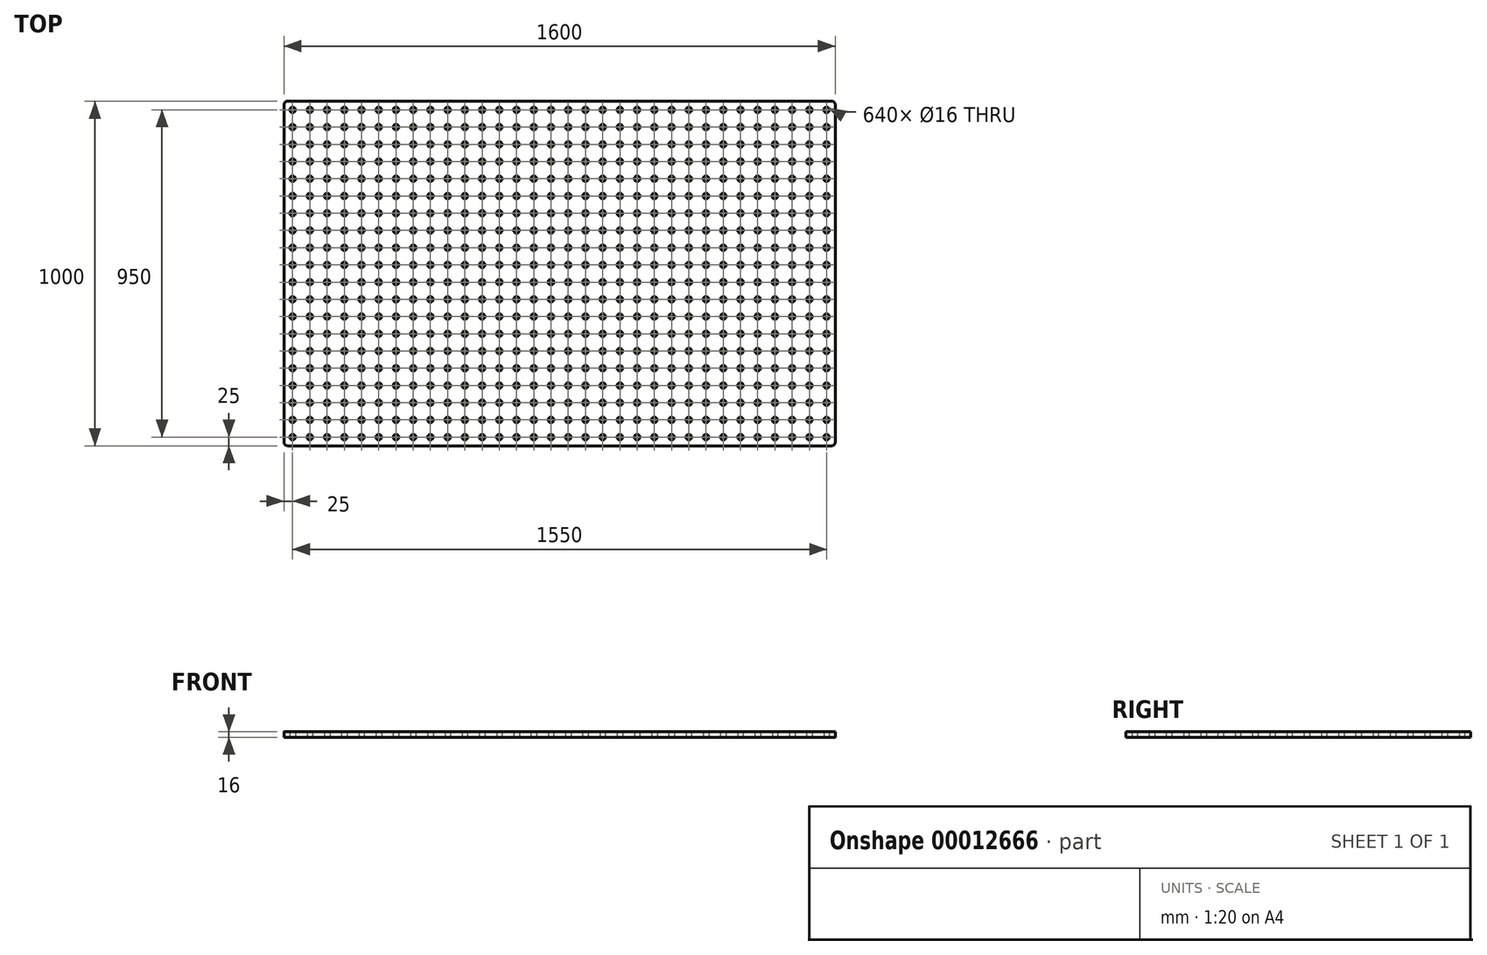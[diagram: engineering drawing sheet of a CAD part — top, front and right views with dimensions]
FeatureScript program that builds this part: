
annotation { "Feature Type Name" : "Feature", "Feature Type Description" : "" }
export const myFeature = defineFeature(function(context is Context, id is Id, definition is map)
    precondition{}
    {
        {
            var Q0;
            Q0=qCreatedBy(makeId("Top.planeOp"),FACE);
            var sketch = newSketch(context, id + "F0", { "sketchPlane" : qUnion([Q0])});
            skLineSegment(sketch, "E0.rect.top", {"start": v(-800, -500) * mm, "end": v(800, -500) * mm});
            skLineSegment(sketch, "E0.rect.left", {"start": v(-800, 500) * mm, "end": v(-800, -500) * mm});
            skLineSegment(sketch, "E0.rect.right", {"start": v(800, 500) * mm, "end": v(800, -500) * mm});
            skPoint(sketch, "E0.rect.middle", {"position": v(0, 0) * mm});
            skCircle(sketch, "E1", {"center": v(-775, 475) * mm, "radius": 8 * mm});
            skCircle(sketch, "E2", {"center": v(-725, 475) * mm, "radius": 8 * mm});
            skCircle(sketch, "E3", {"center": v(-675, 475) * mm, "radius": 8 * mm});
            skCircle(sketch, "E4", {"center": v(-625, 475) * mm, "radius": 8 * mm});
            skCircle(sketch, "E5", {"center": v(-575, 475) * mm, "radius": 8 * mm});
            skCircle(sketch, "E6", {"center": v(-525, 475) * mm, "radius": 8 * mm});
            skCircle(sketch, "E7", {"center": v(-475, 475) * mm, "radius": 8 * mm});
            skCircle(sketch, "E8", {"center": v(-425, 475) * mm, "radius": 8 * mm});
            skCircle(sketch, "E9", {"center": v(-375, 475) * mm, "radius": 8 * mm});
            skCircle(sketch, "E10", {"center": v(-325, 475) * mm, "radius": 8 * mm});
            skCircle(sketch, "E11", {"center": v(-275, 475) * mm, "radius": 8 * mm});
            skCircle(sketch, "E12", {"center": v(-225, 475) * mm, "radius": 8 * mm});
            skCircle(sketch, "E13", {"center": v(-125, 475) * mm, "radius": 8 * mm});
            skCircle(sketch, "E14", {"center": v(-75, 475) * mm, "radius": 8 * mm});
            skCircle(sketch, "E15", {"center": v(-25, 475) * mm, "radius": 8 * mm});
            skCircle(sketch, "E16", {"center": v(25, 475) * mm, "radius": 8 * mm});
            skCircle(sketch, "E17", {"center": v(75, 475) * mm, "radius": 8 * mm});
            skCircle(sketch, "E18", {"center": v(125, 475) * mm, "radius": 8 * mm});
            skCircle(sketch, "E19", {"center": v(175, 475) * mm, "radius": 8 * mm});
            skCircle(sketch, "E20", {"center": v(225, 475) * mm, "radius": 8 * mm});
            skCircle(sketch, "E21", {"center": v(275, 475) * mm, "radius": 8 * mm});
            skCircle(sketch, "E22", {"center": v(325, 475) * mm, "radius": 8 * mm});
            skCircle(sketch, "E23", {"center": v(375, 475) * mm, "radius": 8 * mm});
            skCircle(sketch, "E24", {"center": v(425, 475) * mm, "radius": 8 * mm});
            skCircle(sketch, "E25", {"center": v(475, 475) * mm, "radius": 8 * mm});
            skCircle(sketch, "E26", {"center": v(525, 475) * mm, "radius": 8 * mm});
            skCircle(sketch, "E27", {"center": v(575, 475) * mm, "radius": 8 * mm});
            skCircle(sketch, "E28", {"center": v(625, 475) * mm, "radius": 8 * mm});
            skCircle(sketch, "E29", {"center": v(675, 475) * mm, "radius": 8 * mm});
            skCircle(sketch, "E30", {"center": v(725, 475) * mm, "radius": 8 * mm});
            skCircle(sketch, "E31", {"center": v(775, 475) * mm, "radius": 8 * mm});
            skCircle(sketch, "E32", {"center": v(-175, 475) * mm, "radius": 8 * mm});
            skLineSegment(sketch, "E33", {"start": v(-800, 0) * mm, "end": v(800, 0) * mm, "construction": true});
            skLineSegment(sketch, "E34", {"start": v(-800, 500) * mm, "end": v(800, 500) * mm});
            skCircle(sketch, "E35.0.MirrorC", {"center": v(275, 425) * mm, "radius": 8 * mm});
            skCircle(sketch, "E35.1.MirrorC", {"center": v(725, 425) * mm, "radius": 8 * mm});
            skCircle(sketch, "E35.2.MirrorC", {"center": v(775, 425) * mm, "radius": 8 * mm});
            skCircle(sketch, "E35.3.MirrorC", {"center": v(325, 425) * mm, "radius": 8 * mm});
            skCircle(sketch, "E35.4.MirrorC", {"center": v(-275, 425) * mm, "radius": 8 * mm});
            skCircle(sketch, "E35.5.MirrorC", {"center": v(675, 425) * mm, "radius": 8 * mm});
            skCircle(sketch, "E35.6.MirrorC", {"center": v(575, 425) * mm, "radius": 8 * mm});
            skCircle(sketch, "E35.7.MirrorC", {"center": v(-575, 425) * mm, "radius": 8 * mm});
            skCircle(sketch, "E35.8.MirrorC", {"center": v(-25, 425) * mm, "radius": 8 * mm});
            skCircle(sketch, "E35.9.MirrorC", {"center": v(75, 425) * mm, "radius": 8 * mm});
            skCircle(sketch, "E35.10.MirrorC", {"center": v(-175, 425) * mm, "radius": 8 * mm});
            skCircle(sketch, "E35.11.MirrorC", {"center": v(25, 425) * mm, "radius": 8 * mm});
            skCircle(sketch, "E35.12.MirrorC", {"center": v(175, 425) * mm, "radius": 8 * mm});
            skCircle(sketch, "E35.13.MirrorC", {"center": v(475, 425) * mm, "radius": 8 * mm});
            skCircle(sketch, "E35.14.MirrorC", {"center": v(-525, 425) * mm, "radius": 8 * mm});
            skCircle(sketch, "E35.15.MirrorC", {"center": v(-225, 425) * mm, "radius": 8 * mm});
            skCircle(sketch, "E35.16.MirrorC", {"center": v(-75, 425) * mm, "radius": 8 * mm});
            skCircle(sketch, "E35.17.MirrorC", {"center": v(375, 425) * mm, "radius": 8 * mm});
            skCircle(sketch, "E35.18.MirrorC", {"center": v(-325, 425) * mm, "radius": 8 * mm});
            skCircle(sketch, "E35.19.MirrorC", {"center": v(125, 425) * mm, "radius": 8 * mm});
            skCircle(sketch, "E35.20.MirrorC", {"center": v(-125, 425) * mm, "radius": 8 * mm});
            skCircle(sketch, "E35.21.MirrorC", {"center": v(525, 425) * mm, "radius": 8 * mm});
            skCircle(sketch, "E35.22.MirrorC", {"center": v(225, 425) * mm, "radius": 8 * mm});
            skCircle(sketch, "E35.23.MirrorC", {"center": v(625, 425) * mm, "radius": 8 * mm});
            skCircle(sketch, "E35.24.MirrorC", {"center": v(-725, 425) * mm, "radius": 8 * mm});
            skCircle(sketch, "E35.25.MirrorC", {"center": v(-775, 425) * mm, "radius": 8 * mm});
            skCircle(sketch, "E35.26.MirrorC", {"center": v(-625, 425) * mm, "radius": 8 * mm});
            skCircle(sketch, "E35.27.MirrorC", {"center": v(-675, 425) * mm, "radius": 8 * mm});
            skCircle(sketch, "E35.28.MirrorC", {"center": v(-425, 425) * mm, "radius": 8 * mm});
            skCircle(sketch, "E35.29.MirrorC", {"center": v(-475, 425) * mm, "radius": 8 * mm});
            skCircle(sketch, "E35.30.MirrorC", {"center": v(-375, 425) * mm, "radius": 8 * mm});
            skCircle(sketch, "E35.31.MirrorC", {"center": v(425, 425) * mm, "radius": 8 * mm});
            skCircle(sketch, "E36.0.MirrorC", {"center": v(275, 325) * mm, "radius": 8 * mm});
            skCircle(sketch, "E36.1.MirrorC", {"center": v(375, 375) * mm, "radius": 8 * mm});
            skCircle(sketch, "E36.2.MirrorC", {"center": v(725, 375) * mm, "radius": 8 * mm});
            skCircle(sketch, "E36.3.MirrorC", {"center": v(525, 325) * mm, "radius": 8 * mm});
            skCircle(sketch, "E36.4.MirrorC", {"center": v(575, 375) * mm, "radius": 8 * mm});
            skCircle(sketch, "E36.5.MirrorC", {"center": v(225, 375) * mm, "radius": 8 * mm});
            skCircle(sketch, "E36.6.MirrorC", {"center": v(-775, 375) * mm, "radius": 8 * mm});
            skCircle(sketch, "E36.7.MirrorC", {"center": v(75, 375) * mm, "radius": 8 * mm});
            skCircle(sketch, "E36.8.MirrorC", {"center": v(675, 325) * mm, "radius": 8 * mm});
            skCircle(sketch, "E36.9.MirrorC", {"center": v(425, 375) * mm, "radius": 8 * mm});
            skCircle(sketch, "E36.10.MirrorC", {"center": v(-225, 375) * mm, "radius": 8 * mm});
            skCircle(sketch, "E36.11.MirrorC", {"center": v(175, 325) * mm, "radius": 8 * mm});
            skCircle(sketch, "E36.12.MirrorC", {"center": v(-725, 375) * mm, "radius": 8 * mm});
            skCircle(sketch, "E36.13.MirrorC", {"center": v(625, 325) * mm, "radius": 8 * mm});
            skCircle(sketch, "E36.14.MirrorC", {"center": v(-25, 375) * mm, "radius": 8 * mm});
            skCircle(sketch, "E36.15.MirrorC", {"center": v(-75, 375) * mm, "radius": 8 * mm});
            skCircle(sketch, "E36.16.MirrorC", {"center": v(275, 375) * mm, "radius": 8 * mm});
            skCircle(sketch, "E36.17.MirrorC", {"center": v(225, 325) * mm, "radius": 8 * mm});
            skCircle(sketch, "E36.18.MirrorC", {"center": v(-275, 375) * mm, "radius": 8 * mm});
            skCircle(sketch, "E36.19.MirrorC", {"center": v(-125, 375) * mm, "radius": 8 * mm});
            skCircle(sketch, "E36.20.MirrorC", {"center": v(425, 325) * mm, "radius": 8 * mm});
            skCircle(sketch, "E36.21.MirrorC", {"center": v(-575, 375) * mm, "radius": 8 * mm});
            skCircle(sketch, "E36.22.MirrorC", {"center": v(575, 325) * mm, "radius": 8 * mm});
            skCircle(sketch, "E36.23.MirrorC", {"center": v(625, 375) * mm, "radius": 8 * mm});
            skCircle(sketch, "E36.24.MirrorC", {"center": v(475, 375) * mm, "radius": 8 * mm});
            skCircle(sketch, "E36.25.MirrorC", {"center": v(-475, 375) * mm, "radius": 8 * mm});
            skCircle(sketch, "E36.26.MirrorC", {"center": v(75, 325) * mm, "radius": 8 * mm});
            skCircle(sketch, "E36.27.MirrorC", {"center": v(525, 375) * mm, "radius": 8 * mm});
            skCircle(sketch, "E36.28.MirrorC", {"center": v(675, 375) * mm, "radius": 8 * mm});
            skCircle(sketch, "E36.29.MirrorC", {"center": v(475, 325) * mm, "radius": 8 * mm});
            skCircle(sketch, "E36.30.MirrorC", {"center": v(175, 375) * mm, "radius": 8 * mm});
            skCircle(sketch, "E36.31.MirrorC", {"center": v(-525, 325) * mm, "radius": 8 * mm});
            skCircle(sketch, "E36.32.MirrorC", {"center": v(375, 325) * mm, "radius": 8 * mm});
            skCircle(sketch, "E36.33.MirrorC", {"center": v(125, 375) * mm, "radius": 8 * mm});
            skCircle(sketch, "E36.34.MirrorC", {"center": v(-25, 325) * mm, "radius": 8 * mm});
            skCircle(sketch, "E36.35.MirrorC", {"center": v(125, 325) * mm, "radius": 8 * mm});
            skCircle(sketch, "E36.36.MirrorC", {"center": v(25, 325) * mm, "radius": 8 * mm});
            skCircle(sketch, "E36.37.MirrorC", {"center": v(-425, 375) * mm, "radius": 8 * mm});
            skCircle(sketch, "E36.38.MirrorC", {"center": v(-625, 375) * mm, "radius": 8 * mm});
            skCircle(sketch, "E36.39.MirrorC", {"center": v(775, 325) * mm, "radius": 8 * mm});
            skCircle(sketch, "E36.40.MirrorC", {"center": v(-575, 325) * mm, "radius": 8 * mm});
            skCircle(sketch, "E36.41.MirrorC", {"center": v(-775, 325) * mm, "radius": 8 * mm});
            skCircle(sketch, "E36.42.MirrorC", {"center": v(-725, 325) * mm, "radius": 8 * mm});
            skCircle(sketch, "E36.43.MirrorC", {"center": v(-375, 375) * mm, "radius": 8 * mm});
            skCircle(sketch, "E36.44.MirrorC", {"center": v(-525, 375) * mm, "radius": 8 * mm});
            skCircle(sketch, "E36.45.MirrorC", {"center": v(725, 325) * mm, "radius": 8 * mm});
            skCircle(sketch, "E36.46.MirrorC", {"center": v(-625, 325) * mm, "radius": 8 * mm});
            skCircle(sketch, "E36.47.MirrorC", {"center": v(-175, 325) * mm, "radius": 8 * mm});
            skCircle(sketch, "E36.48.MirrorC", {"center": v(-275, 325) * mm, "radius": 8 * mm});
            skCircle(sketch, "E36.49.MirrorC", {"center": v(-125, 325) * mm, "radius": 8 * mm});
            skCircle(sketch, "E36.50.MirrorC", {"center": v(-225, 325) * mm, "radius": 8 * mm});
            skCircle(sketch, "E36.51.MirrorC", {"center": v(-75, 325) * mm, "radius": 8 * mm});
            skCircle(sketch, "E36.52.MirrorC", {"center": v(325, 325) * mm, "radius": 8 * mm});
            skCircle(sketch, "E36.53.MirrorC", {"center": v(775, 375) * mm, "radius": 8 * mm});
            skCircle(sketch, "E36.54.MirrorC", {"center": v(-325, 375) * mm, "radius": 8 * mm});
            skCircle(sketch, "E36.55.MirrorC", {"center": v(-375, 325) * mm, "radius": 8 * mm});
            skCircle(sketch, "E36.56.MirrorC", {"center": v(-475, 325) * mm, "radius": 8 * mm});
            skCircle(sketch, "E36.57.MirrorC", {"center": v(-325, 325) * mm, "radius": 8 * mm});
            skCircle(sketch, "E36.58.MirrorC", {"center": v(-675, 375) * mm, "radius": 8 * mm});
            skCircle(sketch, "E36.59.MirrorC", {"center": v(25, 375) * mm, "radius": 8 * mm});
            skCircle(sketch, "E36.60.MirrorC", {"center": v(-175, 375) * mm, "radius": 8 * mm});
            skCircle(sketch, "E36.61.MirrorC", {"center": v(-675, 325) * mm, "radius": 8 * mm});
            skCircle(sketch, "E36.62.MirrorC", {"center": v(325, 375) * mm, "radius": 8 * mm});
            skCircle(sketch, "E36.63.MirrorC", {"center": v(-425, 325) * mm, "radius": 8 * mm});
            skCircle(sketch, "E37.0.MirrorC", {"center": v(-675, 275) * mm, "radius": 8 * mm});
            skCircle(sketch, "E37.1.MirrorC", {"center": v(475, 275) * mm, "radius": 8 * mm});
            skCircle(sketch, "E37.2.MirrorC", {"center": v(725, 275) * mm, "radius": 8 * mm});
            skCircle(sketch, "E37.3.MirrorC", {"center": v(425, 175) * mm, "radius": 8 * mm});
            skCircle(sketch, "E37.4.MirrorC", {"center": v(625, 275) * mm, "radius": 8 * mm});
            skCircle(sketch, "E37.5.MirrorC", {"center": v(-225, 175) * mm, "radius": 8 * mm});
            skCircle(sketch, "E37.6.MirrorC", {"center": v(175, 125) * mm, "radius": 8 * mm});
            skCircle(sketch, "E37.7.MirrorC", {"center": v(-25, 225) * mm, "radius": 8 * mm});
            skCircle(sketch, "E37.8.MirrorC", {"center": v(-75, 175) * mm, "radius": 8 * mm});
            skCircle(sketch, "E37.9.MirrorC", {"center": v(275, 175) * mm, "radius": 8 * mm});
            skCircle(sketch, "E37.10.MirrorC", {"center": v(225, 125) * mm, "radius": 8 * mm});
            skCircle(sketch, "E37.11.MirrorC", {"center": v(325, 225) * mm, "radius": 8 * mm});
            skCircle(sketch, "E37.12.MirrorC", {"center": v(-625, 275) * mm, "radius": 8 * mm});
            skCircle(sketch, "E37.13.MirrorC", {"center": v(175, 225) * mm, "radius": 8 * mm});
            skCircle(sketch, "E37.14.MirrorC", {"center": v(-375, 225) * mm, "radius": 8 * mm});
            skCircle(sketch, "E37.15.MirrorC", {"center": v(525, 225) * mm, "radius": 8 * mm});
            skCircle(sketch, "E37.16.MirrorC", {"center": v(25, 225) * mm, "radius": 8 * mm});
            skCircle(sketch, "E37.17.MirrorC", {"center": v(475, 175) * mm, "radius": 8 * mm});
            skCircle(sketch, "E37.18.MirrorC", {"center": v(175, 275) * mm, "radius": 8 * mm});
            skCircle(sketch, "E37.19.MirrorC", {"center": v(-475, 175) * mm, "radius": 8 * mm});
            skCircle(sketch, "E37.20.MirrorC", {"center": v(75, 125) * mm, "radius": 8 * mm});
            skCircle(sketch, "E37.21.MirrorC", {"center": v(675, 225) * mm, "radius": 8 * mm});
            skCircle(sketch, "E37.22.MirrorC", {"center": v(-525, 225) * mm, "radius": 8 * mm});
            skCircle(sketch, "E37.23.MirrorC", {"center": v(-175, 225) * mm, "radius": 8 * mm});
            skCircle(sketch, "E37.24.MirrorC", {"center": v(-525, 175) * mm, "radius": 8 * mm});
            skCircle(sketch, "E37.25.MirrorC", {"center": v(-725, 225) * mm, "radius": 8 * mm});
            skCircle(sketch, "E37.26.MirrorC", {"center": v(-375, 175) * mm, "radius": 8 * mm});
            skCircle(sketch, "E37.27.MirrorC", {"center": v(125, 125) * mm, "radius": 8 * mm});
            skCircle(sketch, "E37.28.MirrorC", {"center": v(-425, 275) * mm, "radius": 8 * mm});
            skCircle(sketch, "E37.29.MirrorC", {"center": v(-275, 125) * mm, "radius": 8 * mm});
            skCircle(sketch, "E37.30.MirrorC", {"center": v(-125, 125) * mm, "radius": 8 * mm});
            skCircle(sketch, "E37.31.MirrorC", {"center": v(-225, 125) * mm, "radius": 8 * mm});
            skCircle(sketch, "E37.32.MirrorC", {"center": v(275, 225) * mm, "radius": 8 * mm});
            skCircle(sketch, "E37.33.MirrorC", {"center": v(275, 275) * mm, "radius": 8 * mm});
            skCircle(sketch, "E37.34.MirrorC", {"center": v(-275, 275) * mm, "radius": 8 * mm});
            skCircle(sketch, "E37.35.MirrorC", {"center": v(375, 275) * mm, "radius": 8 * mm});
            skCircle(sketch, "E37.36.MirrorC", {"center": v(325, 125) * mm, "radius": 8 * mm});
            skCircle(sketch, "E37.37.MirrorC", {"center": v(-325, 175) * mm, "radius": 8 * mm});
            skCircle(sketch, "E37.38.MirrorC", {"center": v(775, 175) * mm, "radius": 8 * mm});
            skCircle(sketch, "E37.39.MirrorC", {"center": v(-375, 125) * mm, "radius": 8 * mm});
            skCircle(sketch, "E37.40.MirrorC", {"center": v(-325, 125) * mm, "radius": 8 * mm});
            skCircle(sketch, "E37.41.MirrorC", {"center": v(-475, 125) * mm, "radius": 8 * mm});
            skCircle(sketch, "E37.42.MirrorC", {"center": v(-425, 125) * mm, "radius": 8 * mm});
            skCircle(sketch, "E37.43.MirrorC", {"center": v(-575, 125) * mm, "radius": 8 * mm});
            skCircle(sketch, "E37.44.MirrorC", {"center": v(-525, 125) * mm, "radius": 8 * mm});
            skCircle(sketch, "E37.45.MirrorC", {"center": v(-675, 125) * mm, "radius": 8 * mm});
            skCircle(sketch, "E37.46.MirrorC", {"center": v(-625, 125) * mm, "radius": 8 * mm});
            skCircle(sketch, "E37.47.MirrorC", {"center": v(-775, 125) * mm, "radius": 8 * mm});
            skCircle(sketch, "E37.48.MirrorC", {"center": v(-725, 125) * mm, "radius": 8 * mm});
            skCircle(sketch, "E37.49.MirrorC", {"center": v(325, 175) * mm, "radius": 8 * mm});
            skCircle(sketch, "E37.50.MirrorC", {"center": v(375, 125) * mm, "radius": 8 * mm});
            skCircle(sketch, "E37.51.MirrorC", {"center": v(125, 175) * mm, "radius": 8 * mm});
            skCircle(sketch, "E37.52.MirrorC", {"center": v(375, 225) * mm, "radius": 8 * mm});
            skCircle(sketch, "E37.53.MirrorC", {"center": v(225, 275) * mm, "radius": 8 * mm});
            skCircle(sketch, "E37.54.MirrorC", {"center": v(125, 225) * mm, "radius": 8 * mm});
            skCircle(sketch, "E37.55.MirrorC", {"center": v(-575, 225) * mm, "radius": 8 * mm});
            skCircle(sketch, "E37.56.MirrorC", {"center": v(-425, 225) * mm, "radius": 8 * mm});
            skCircle(sketch, "E37.57.MirrorC", {"center": v(775, 225) * mm, "radius": 8 * mm});
            skCircle(sketch, "E37.58.MirrorC", {"center": v(625, 175) * mm, "radius": 8 * mm});
            skCircle(sketch, "E37.59.MirrorC", {"center": v(225, 225) * mm, "radius": 8 * mm});
            skCircle(sketch, "E37.60.MirrorC", {"center": v(575, 125) * mm, "radius": 8 * mm});
            skCircle(sketch, "E37.61.MirrorC", {"center": v(-575, 175) * mm, "radius": 8 * mm});
            skCircle(sketch, "E37.62.MirrorC", {"center": v(425, 125) * mm, "radius": 8 * mm});
            skCircle(sketch, "E37.63.MirrorC", {"center": v(-125, 175) * mm, "radius": 8 * mm});
            skCircle(sketch, "E37.64.MirrorC", {"center": v(-275, 175) * mm, "radius": 8 * mm});
            skCircle(sketch, "E37.65.MirrorC", {"center": v(725, 225) * mm, "radius": 8 * mm});
            skCircle(sketch, "E37.66.MirrorC", {"center": v(-275, 225) * mm, "radius": 8 * mm});
            skCircle(sketch, "E37.67.MirrorC", {"center": v(-25, 275) * mm, "radius": 8 * mm});
            skCircle(sketch, "E37.68.MirrorC", {"center": v(-225, 275) * mm, "radius": 8 * mm});
            skCircle(sketch, "E37.69.MirrorC", {"center": v(475, 225) * mm, "radius": 8 * mm});
            skCircle(sketch, "E37.70.MirrorC", {"center": v(-575, 275) * mm, "radius": 8 * mm});
            skCircle(sketch, "E37.71.MirrorC", {"center": v(-475, 275) * mm, "radius": 8 * mm});
            skCircle(sketch, "E37.72.MirrorC", {"center": v(675, 275) * mm, "radius": 8 * mm});
            skCircle(sketch, "E37.73.MirrorC", {"center": v(-625, 175) * mm, "radius": 8 * mm});
            skCircle(sketch, "E37.74.MirrorC", {"center": v(-175, 175) * mm, "radius": 8 * mm});
            skCircle(sketch, "E37.75.MirrorC", {"center": v(725, 125) * mm, "radius": 8 * mm});
            skCircle(sketch, "E37.76.MirrorC", {"center": v(-75, 125) * mm, "radius": 8 * mm});
            skCircle(sketch, "E37.77.MirrorC", {"center": v(-25, 175) * mm, "radius": 8 * mm});
            skCircle(sketch, "E37.78.MirrorC", {"center": v(625, 125) * mm, "radius": 8 * mm});
            skCircle(sketch, "E37.79.MirrorC", {"center": v(-775, 225) * mm, "radius": 8 * mm});
            skCircle(sketch, "E37.80.MirrorC", {"center": v(-725, 175) * mm, "radius": 8 * mm});
            skCircle(sketch, "E37.81.MirrorC", {"center": v(-625, 225) * mm, "radius": 8 * mm});
            skCircle(sketch, "E37.82.MirrorC", {"center": v(575, 275) * mm, "radius": 8 * mm});
            skCircle(sketch, "E37.83.MirrorC", {"center": v(-325, 225) * mm, "radius": 8 * mm});
            skCircle(sketch, "E37.84.MirrorC", {"center": v(675, 125) * mm, "radius": 8 * mm});
            skCircle(sketch, "E37.85.MirrorC", {"center": v(-125, 225) * mm, "radius": 8 * mm});
            skCircle(sketch, "E37.86.MirrorC", {"center": v(-775, 275) * mm, "radius": 8 * mm});
            skCircle(sketch, "E37.87.MirrorC", {"center": v(125, 275) * mm, "radius": 8 * mm});
            skCircle(sketch, "E37.88.MirrorC", {"center": v(-25, 125) * mm, "radius": 8 * mm});
            skCircle(sketch, "E37.89.MirrorC", {"center": v(425, 225) * mm, "radius": 8 * mm});
            skCircle(sketch, "E37.90.MirrorC", {"center": v(25, 125) * mm, "radius": 8 * mm});
            skCircle(sketch, "E37.91.MirrorC", {"center": v(-675, 225) * mm, "radius": 8 * mm});
            skCircle(sketch, "E37.92.MirrorC", {"center": v(75, 175) * mm, "radius": 8 * mm});
            skCircle(sketch, "E37.93.MirrorC", {"center": v(275, 125) * mm, "radius": 8 * mm});
            skCircle(sketch, "E37.94.MirrorC", {"center": v(525, 125) * mm, "radius": 8 * mm});
            skCircle(sketch, "E37.95.MirrorC", {"center": v(175, 175) * mm, "radius": 8 * mm});
            skCircle(sketch, "E37.96.MirrorC", {"center": v(-225, 225) * mm, "radius": 8 * mm});
            skCircle(sketch, "E37.97.MirrorC", {"center": v(-175, 275) * mm, "radius": 8 * mm});
            skCircle(sketch, "E37.98.MirrorC", {"center": v(-125, 275) * mm, "radius": 8 * mm});
            skCircle(sketch, "E37.99.MirrorC", {"center": v(475, 125) * mm, "radius": 8 * mm});
            skCircle(sketch, "E37.100.MirrorC", {"center": v(775, 275) * mm, "radius": 8 * mm});
            skCircle(sketch, "E37.101.MirrorC", {"center": v(-775, 175) * mm, "radius": 8 * mm});
            skCircle(sketch, "E37.102.MirrorC", {"center": v(775, 125) * mm, "radius": 8 * mm});
            skCircle(sketch, "E37.103.MirrorC", {"center": v(-375, 275) * mm, "radius": 8 * mm});
            skCircle(sketch, "E37.104.MirrorC", {"center": v(725, 175) * mm, "radius": 8 * mm});
            skCircle(sketch, "E37.105.MirrorC", {"center": v(675, 175) * mm, "radius": 8 * mm});
            skCircle(sketch, "E37.106.MirrorC", {"center": v(625, 225) * mm, "radius": 8 * mm});
            skCircle(sketch, "E37.107.MirrorC", {"center": v(375, 175) * mm, "radius": 8 * mm});
            skCircle(sketch, "E37.108.MirrorC", {"center": v(-75, 225) * mm, "radius": 8 * mm});
            skCircle(sketch, "E37.109.MirrorC", {"center": v(-425, 175) * mm, "radius": 8 * mm});
            skCircle(sketch, "E37.110.MirrorC", {"center": v(-75, 275) * mm, "radius": 8 * mm});
            skCircle(sketch, "E37.111.MirrorC", {"center": v(-325, 275) * mm, "radius": 8 * mm});
            skCircle(sketch, "E37.112.MirrorC", {"center": v(-475, 225) * mm, "radius": 8 * mm});
            skCircle(sketch, "E37.113.MirrorC", {"center": v(-675, 175) * mm, "radius": 8 * mm});
            skCircle(sketch, "E37.114.MirrorC", {"center": v(-525, 275) * mm, "radius": 8 * mm});
            skCircle(sketch, "E37.115.MirrorC", {"center": v(525, 275) * mm, "radius": 8 * mm});
            skCircle(sketch, "E37.116.MirrorC", {"center": v(525, 175) * mm, "radius": 8 * mm});
            skCircle(sketch, "E37.117.MirrorC", {"center": v(325, 275) * mm, "radius": 8 * mm});
            skCircle(sketch, "E37.118.MirrorC", {"center": v(25, 175) * mm, "radius": 8 * mm});
            skCircle(sketch, "E37.119.MirrorC", {"center": v(25, 275) * mm, "radius": 8 * mm});
            skCircle(sketch, "E37.120.MirrorC", {"center": v(425, 275) * mm, "radius": 8 * mm});
            skCircle(sketch, "E37.121.MirrorC", {"center": v(575, 225) * mm, "radius": 8 * mm});
            skCircle(sketch, "E37.122.MirrorC", {"center": v(575, 175) * mm, "radius": 8 * mm});
            skCircle(sketch, "E37.123.MirrorC", {"center": v(225, 175) * mm, "radius": 8 * mm});
            skCircle(sketch, "E37.124.MirrorC", {"center": v(-725, 275) * mm, "radius": 8 * mm});
            skCircle(sketch, "E37.125.MirrorC", {"center": v(75, 275) * mm, "radius": 8 * mm});
            skCircle(sketch, "E37.126.MirrorC", {"center": v(-175, 125) * mm, "radius": 8 * mm});
            skCircle(sketch, "E37.127.MirrorC", {"center": v(75, 225) * mm, "radius": 8 * mm});
            skCircle(sketch, "E38.0.MirrorC", {"center": v(75, 25) * mm, "radius": 8 * mm});
            skCircle(sketch, "E38.1.MirrorC", {"center": v(-75, 75) * mm, "radius": 8 * mm});
            skCircle(sketch, "E38.2.MirrorC", {"center": v(575, 75) * mm, "radius": 8 * mm});
            skCircle(sketch, "E38.3.MirrorC", {"center": v(-525, 75) * mm, "radius": 8 * mm});
            skCircle(sketch, "E38.4.MirrorC", {"center": v(-25, 25) * mm, "radius": 8 * mm});
            skCircle(sketch, "E38.5.MirrorC", {"center": v(-575, 25) * mm, "radius": 8 * mm});
            skCircle(sketch, "E38.6.MirrorC", {"center": v(-675, 75) * mm, "radius": 8 * mm});
            skCircle(sketch, "E38.7.MirrorC", {"center": v(-275, 75) * mm, "radius": 8 * mm});
            skCircle(sketch, "E38.8.MirrorC", {"center": v(275, 75) * mm, "radius": 8 * mm});
            skCircle(sketch, "E38.9.MirrorC", {"center": v(-425, 25) * mm, "radius": 8 * mm});
            skCircle(sketch, "E38.10.MirrorC", {"center": v(25, 75) * mm, "radius": 8 * mm});
            skCircle(sketch, "E38.11.MirrorC", {"center": v(575, 25) * mm, "radius": 8 * mm});
            skCircle(sketch, "E38.12.MirrorC", {"center": v(-425, 75) * mm, "radius": 8 * mm});
            skCircle(sketch, "E38.13.MirrorC", {"center": v(-375, 25) * mm, "radius": 8 * mm});
            skCircle(sketch, "E38.14.MirrorC", {"center": v(-175, 25) * mm, "radius": 8 * mm});
            skCircle(sketch, "E38.15.MirrorC", {"center": v(625, 25) * mm, "radius": 8 * mm});
            skCircle(sketch, "E38.16.MirrorC", {"center": v(225, 75) * mm, "radius": 8 * mm});
            skCircle(sketch, "E38.17.MirrorC", {"center": v(125, 75) * mm, "radius": 8 * mm});
            skCircle(sketch, "E38.18.MirrorC", {"center": v(-575, 75) * mm, "radius": 8 * mm});
            skCircle(sketch, "E38.19.MirrorC", {"center": v(725, 75) * mm, "radius": 8 * mm});
            skCircle(sketch, "E38.20.MirrorC", {"center": v(375, 25) * mm, "radius": 8 * mm});
            skCircle(sketch, "E38.21.MirrorC", {"center": v(225, 25) * mm, "radius": 8 * mm});
            skCircle(sketch, "E38.22.MirrorC", {"center": v(-175, 75) * mm, "radius": 8 * mm});
            skCircle(sketch, "E38.23.MirrorC", {"center": v(525, 75) * mm, "radius": 8 * mm});
            skCircle(sketch, "E38.24.MirrorC", {"center": v(425, 75) * mm, "radius": 8 * mm});
            skCircle(sketch, "E38.25.MirrorC", {"center": v(625, 75) * mm, "radius": 8 * mm});
            skCircle(sketch, "E38.26.MirrorC", {"center": v(-125, 75) * mm, "radius": 8 * mm});
            skCircle(sketch, "E38.27.MirrorC", {"center": v(-625, 75) * mm, "radius": 8 * mm});
            skCircle(sketch, "E38.28.MirrorC", {"center": v(-775, 75) * mm, "radius": 8 * mm});
            skCircle(sketch, "E38.29.MirrorC", {"center": v(-225, 75) * mm, "radius": 8 * mm});
            skCircle(sketch, "E38.30.MirrorC", {"center": v(175, 25) * mm, "radius": 8 * mm});
            skCircle(sketch, "E38.31.MirrorC", {"center": v(-125, 25) * mm, "radius": 8 * mm});
            skCircle(sketch, "E38.32.MirrorC", {"center": v(-725, 75) * mm, "radius": 8 * mm});
            skCircle(sketch, "E38.33.MirrorC", {"center": v(-275, 25) * mm, "radius": 8 * mm});
            skCircle(sketch, "E38.34.MirrorC", {"center": v(-725, 25) * mm, "radius": 8 * mm});
            skCircle(sketch, "E38.35.MirrorC", {"center": v(425, 25) * mm, "radius": 8 * mm});
            skCircle(sketch, "E38.36.MirrorC", {"center": v(-475, 25) * mm, "radius": 8 * mm});
            skCircle(sketch, "E38.37.MirrorC", {"center": v(125, 25) * mm, "radius": 8 * mm});
            skCircle(sketch, "E38.38.MirrorC", {"center": v(475, 75) * mm, "radius": 8 * mm});
            skCircle(sketch, "E38.39.MirrorC", {"center": v(-375, 75) * mm, "radius": 8 * mm});
            skCircle(sketch, "E38.40.MirrorC", {"center": v(725, 25) * mm, "radius": 8 * mm});
            skCircle(sketch, "E38.41.MirrorC", {"center": v(-25, 75) * mm, "radius": 8 * mm});
            skCircle(sketch, "E38.42.MirrorC", {"center": v(-325, 75) * mm, "radius": 8 * mm});
            skCircle(sketch, "E38.43.MirrorC", {"center": v(-525, 25) * mm, "radius": 8 * mm});
            skCircle(sketch, "E38.44.MirrorC", {"center": v(-75, 25) * mm, "radius": 8 * mm});
            skCircle(sketch, "E38.45.MirrorC", {"center": v(675, 25) * mm, "radius": 8 * mm});
            skCircle(sketch, "E38.46.MirrorC", {"center": v(-475, 75) * mm, "radius": 8 * mm});
            skCircle(sketch, "E38.47.MirrorC", {"center": v(-625, 25) * mm, "radius": 8 * mm});
            skCircle(sketch, "E38.48.MirrorC", {"center": v(275, 25) * mm, "radius": 8 * mm});
            skCircle(sketch, "E38.49.MirrorC", {"center": v(325, 75) * mm, "radius": 8 * mm});
            skCircle(sketch, "E38.50.MirrorC", {"center": v(75, 75) * mm, "radius": 8 * mm});
            skCircle(sketch, "E38.51.MirrorC", {"center": v(525, 25) * mm, "radius": 8 * mm});
            skCircle(sketch, "E38.52.MirrorC", {"center": v(675, 75) * mm, "radius": 8 * mm});
            skCircle(sketch, "E38.53.MirrorC", {"center": v(-225, 25) * mm, "radius": 8 * mm});
            skCircle(sketch, "E38.54.MirrorC", {"center": v(-325, 25) * mm, "radius": 8 * mm});
            skCircle(sketch, "E38.55.MirrorC", {"center": v(-775, 25) * mm, "radius": 8 * mm});
            skCircle(sketch, "E38.56.MirrorC", {"center": v(375, 75) * mm, "radius": 8 * mm});
            skCircle(sketch, "E38.57.MirrorC", {"center": v(325, 25) * mm, "radius": 8 * mm});
            skCircle(sketch, "E38.58.MirrorC", {"center": v(475, 25) * mm, "radius": 8 * mm});
            skCircle(sketch, "E38.59.MirrorC", {"center": v(-675, 25) * mm, "radius": 8 * mm});
            skCircle(sketch, "E38.60.MirrorC", {"center": v(25, 25) * mm, "radius": 8 * mm});
            skCircle(sketch, "E38.61.MirrorC", {"center": v(775, 75) * mm, "radius": 8 * mm});
            skCircle(sketch, "E38.62.MirrorC", {"center": v(775, 25) * mm, "radius": 8 * mm});
            skCircle(sketch, "E38.63.MirrorC", {"center": v(175, 75) * mm, "radius": 8 * mm});
            skCircle(sketch, "E39.0.MirrorC", {"center": v(125, -125) * mm, "radius": 8 * mm});
            skCircle(sketch, "E39.1.MirrorC", {"center": v(-575, -125) * mm, "radius": 8 * mm});
            skCircle(sketch, "E39.2.MirrorC", {"center": v(225, -225) * mm, "radius": 8 * mm});
            skCircle(sketch, "E39.3.MirrorC", {"center": v(725, -125) * mm, "radius": 8 * mm});
            skCircle(sketch, "E39.4.MirrorC", {"center": v(525, -375) * mm, "radius": 8 * mm});
            skCircle(sketch, "E39.5.MirrorC", {"center": v(-375, -375) * mm, "radius": 8 * mm});
            skCircle(sketch, "E39.6.MirrorC", {"center": v(25, -375) * mm, "radius": 8 * mm});
            skCircle(sketch, "E39.7.MirrorC", {"center": v(325, -225) * mm, "radius": 8 * mm});
            skCircle(sketch, "E39.8.MirrorC", {"center": v(-525, -25) * mm, "radius": 8 * mm});
            skCircle(sketch, "E39.9.MirrorC", {"center": v(-625, -75) * mm, "radius": 8 * mm});
            skCircle(sketch, "E39.10.MirrorC", {"center": v(-675, -225) * mm, "radius": 8 * mm});
            skCircle(sketch, "E39.11.MirrorC", {"center": v(-675, -25) * mm, "radius": 8 * mm});
            skCircle(sketch, "E39.12.MirrorC", {"center": v(375, -175) * mm, "radius": 8 * mm});
            skCircle(sketch, "E39.13.MirrorC", {"center": v(225, -175) * mm, "radius": 8 * mm});
            skCircle(sketch, "E39.14.MirrorC", {"center": v(575, -25) * mm, "radius": 8 * mm});
            skCircle(sketch, "E39.15.MirrorC", {"center": v(175, -325) * mm, "radius": 8 * mm});
            skCircle(sketch, "E39.16.MirrorC", {"center": v(-675, -425) * mm, "radius": 8 * mm});
            skCircle(sketch, "E39.17.MirrorC", {"center": v(25, -425) * mm, "radius": 8 * mm});
            skCircle(sketch, "E39.18.MirrorC", {"center": v(725, -475) * mm, "radius": 8 * mm});
            skCircle(sketch, "E39.19.MirrorC", {"center": v(-75, -475) * mm, "radius": 8 * mm});
            skCircle(sketch, "E39.20.MirrorC", {"center": v(25, -25) * mm, "radius": 8 * mm});
            skCircle(sketch, "E39.21.MirrorC", {"center": v(-75, -25) * mm, "radius": 8 * mm});
            skCircle(sketch, "E39.22.MirrorC", {"center": v(-775, -75) * mm, "radius": 8 * mm});
            skCircle(sketch, "E39.23.MirrorC", {"center": v(-425, -75) * mm, "radius": 8 * mm});
            skCircle(sketch, "E39.24.MirrorC", {"center": v(-725, -275) * mm, "radius": 8 * mm});
            skCircle(sketch, "E39.25.MirrorC", {"center": v(-75, -225) * mm, "radius": 8 * mm});
            skCircle(sketch, "E39.26.MirrorC", {"center": v(75, -175) * mm, "radius": 8 * mm});
            skCircle(sketch, "E39.27.MirrorC", {"center": v(-75, -125) * mm, "radius": 8 * mm});
            skCircle(sketch, "E39.28.MirrorC", {"center": v(575, -125) * mm, "radius": 8 * mm});
            skCircle(sketch, "E39.29.MirrorC", {"center": v(-525, -125) * mm, "radius": 8 * mm});
            skCircle(sketch, "E39.30.MirrorC", {"center": v(-425, -275) * mm, "radius": 8 * mm});
            skCircle(sketch, "E39.31.MirrorC", {"center": v(675, -375) * mm, "radius": 8 * mm});
            skCircle(sketch, "E39.32.MirrorC", {"center": v(-525, -375) * mm, "radius": 8 * mm});
            skCircle(sketch, "E39.33.MirrorC", {"center": v(-175, -375) * mm, "radius": 8 * mm});
            skCircle(sketch, "E39.34.MirrorC", {"center": v(-625, -275) * mm, "radius": 8 * mm});
            skCircle(sketch, "E39.35.MirrorC", {"center": v(775, -475) * mm, "radius": 8 * mm});
            skCircle(sketch, "E39.36.MirrorC", {"center": v(175, -425) * mm, "radius": 8 * mm});
            skCircle(sketch, "E39.37.MirrorC", {"center": v(-425, -425) * mm, "radius": 8 * mm});
            skCircle(sketch, "E39.38.MirrorC", {"center": v(-725, -375) * mm, "radius": 8 * mm});
            skCircle(sketch, "E39.39.MirrorC", {"center": v(-25, -475) * mm, "radius": 8 * mm});
            skCircle(sketch, "E39.40.MirrorC", {"center": v(775, -75) * mm, "radius": 8 * mm});
            skCircle(sketch, "E39.41.MirrorC", {"center": v(-225, -75) * mm, "radius": 8 * mm});
            skCircle(sketch, "E39.42.MirrorC", {"center": v(675, -25) * mm, "radius": 8 * mm});
            skCircle(sketch, "E39.43.MirrorC", {"center": v(75, -275) * mm, "radius": 8 * mm});
            skCircle(sketch, "E39.44.MirrorC", {"center": v(-375, -25) * mm, "radius": 8 * mm});
            skCircle(sketch, "E39.45.MirrorC", {"center": v(275, -125) * mm, "radius": 8 * mm});
            skCircle(sketch, "E39.46.MirrorC", {"center": v(-425, -175) * mm, "radius": 8 * mm});
            skCircle(sketch, "E39.47.MirrorC", {"center": v(475, -425) * mm, "radius": 8 * mm});
            skCircle(sketch, "E39.48.MirrorC", {"center": v(-175, -475) * mm, "radius": 8 * mm});
            skCircle(sketch, "E39.49.MirrorC", {"center": v(625, -325) * mm, "radius": 8 * mm});
            skCircle(sketch, "E39.50.MirrorC", {"center": v(-475, -425) * mm, "radius": 8 * mm});
            skCircle(sketch, "E39.51.MirrorC", {"center": v(25, -475) * mm, "radius": 8 * mm});
            skCircle(sketch, "E39.52.MirrorC", {"center": v(-675, -125) * mm, "radius": 8 * mm});
            skCircle(sketch, "E39.53.MirrorC", {"center": v(-275, -125) * mm, "radius": 8 * mm});
            skCircle(sketch, "E39.54.MirrorC", {"center": v(-25, -175) * mm, "radius": 8 * mm});
            skCircle(sketch, "E39.55.MirrorC", {"center": v(-575, -175) * mm, "radius": 8 * mm});
            skCircle(sketch, "E39.56.MirrorC", {"center": v(725, -325) * mm, "radius": 8 * mm});
            skCircle(sketch, "E39.57.MirrorC", {"center": v(475, -325) * mm, "radius": 8 * mm});
            skCircle(sketch, "E39.58.MirrorC", {"center": v(175, -225) * mm, "radius": 8 * mm});
            skCircle(sketch, "E39.59.MirrorC", {"center": v(-675, -325) * mm, "radius": 8 * mm});
            skCircle(sketch, "E39.60.MirrorC", {"center": v(-75, -175) * mm, "radius": 8 * mm});
            skCircle(sketch, "E39.61.MirrorC", {"center": v(-475, -325) * mm, "radius": 8 * mm});
            skCircle(sketch, "E39.62.MirrorC", {"center": v(-575, -325) * mm, "radius": 8 * mm});
            skCircle(sketch, "E39.63.MirrorC", {"center": v(475, -375) * mm, "radius": 8 * mm});
            skCircle(sketch, "E39.64.MirrorC", {"center": v(675, -275) * mm, "radius": 8 * mm});
            skCircle(sketch, "E39.65.MirrorC", {"center": v(-425, -225) * mm, "radius": 8 * mm});
            skCircle(sketch, "E39.66.MirrorC", {"center": v(-525, -175) * mm, "radius": 8 * mm});
            skCircle(sketch, "E39.67.MirrorC", {"center": v(-325, -125) * mm, "radius": 8 * mm});
            skCircle(sketch, "E39.68.MirrorC", {"center": v(425, -275) * mm, "radius": 8 * mm});
            skCircle(sketch, "E39.69.MirrorC", {"center": v(275, -75) * mm, "radius": 8 * mm});
            skCircle(sketch, "E39.70.MirrorC", {"center": v(725, -175) * mm, "radius": 8 * mm});
            skCircle(sketch, "E39.71.MirrorC", {"center": v(-25, -125) * mm, "radius": 8 * mm});
            skCircle(sketch, "E39.72.MirrorC", {"center": v(375, -75) * mm, "radius": 8 * mm});
            skCircle(sketch, "E39.73.MirrorC", {"center": v(725, -25) * mm, "radius": 8 * mm});
            skCircle(sketch, "E39.74.MirrorC", {"center": v(425, -75) * mm, "radius": 8 * mm});
            skCircle(sketch, "E39.75.MirrorC", {"center": v(-725, -425) * mm, "radius": 8 * mm});
            skCircle(sketch, "E39.76.MirrorC", {"center": v(675, -325) * mm, "radius": 8 * mm});
            skCircle(sketch, "E39.77.MirrorC", {"center": v(575, -475) * mm, "radius": 8 * mm});
            skCircle(sketch, "E39.78.MirrorC", {"center": v(-25, -425) * mm, "radius": 8 * mm});
            skCircle(sketch, "E39.79.MirrorC", {"center": v(-675, -275) * mm, "radius": 8 * mm});
            skCircle(sketch, "E39.80.MirrorC", {"center": v(25, -225) * mm, "radius": 8 * mm});
            skCircle(sketch, "E39.81.MirrorC", {"center": v(375, -325) * mm, "radius": 8 * mm});
            skCircle(sketch, "E39.82.MirrorC", {"center": v(-275, -325) * mm, "radius": 8 * mm});
            skCircle(sketch, "E39.83.MirrorC", {"center": v(275, -325) * mm, "radius": 8 * mm});
            skCircle(sketch, "E39.84.MirrorC", {"center": v(275, -375) * mm, "radius": 8 * mm});
            skCircle(sketch, "E39.85.MirrorC", {"center": v(275, -425) * mm, "radius": 8 * mm});
            skCircle(sketch, "E39.86.MirrorC", {"center": v(-75, -425) * mm, "radius": 8 * mm});
            skCircle(sketch, "E39.87.MirrorC", {"center": v(175, -475) * mm, "radius": 8 * mm});
            skCircle(sketch, "E39.88.MirrorC", {"center": v(275, -25) * mm, "radius": 8 * mm});
            skCircle(sketch, "E39.89.MirrorC", {"center": v(-725, -75) * mm, "radius": 8 * mm});
            skCircle(sketch, "E39.90.MirrorC", {"center": v(225, -75) * mm, "radius": 8 * mm});
            skCircle(sketch, "E39.91.MirrorC", {"center": v(75, -25) * mm, "radius": 8 * mm});
            skCircle(sketch, "E39.92.MirrorC", {"center": v(-475, -225) * mm, "radius": 8 * mm});
            skCircle(sketch, "E39.93.MirrorC", {"center": v(-225, -225) * mm, "radius": 8 * mm});
            skCircle(sketch, "E39.94.MirrorC", {"center": v(-725, -175) * mm, "radius": 8 * mm});
            skCircle(sketch, "E39.95.MirrorC", {"center": v(-275, -175) * mm, "radius": 8 * mm});
            skCircle(sketch, "E39.96.MirrorC", {"center": v(-725, -125) * mm, "radius": 8 * mm});
            skCircle(sketch, "E39.97.MirrorC", {"center": v(275, -225) * mm, "radius": 8 * mm});
            skCircle(sketch, "E39.98.MirrorC", {"center": v(225, -325) * mm, "radius": 8 * mm});
            skCircle(sketch, "E39.99.MirrorC", {"center": v(375, -375) * mm, "radius": 8 * mm});
            skCircle(sketch, "E39.100.MirrorC", {"center": v(375, -425) * mm, "radius": 8 * mm});
            skCircle(sketch, "E39.101.MirrorC", {"center": v(725, -425) * mm, "radius": 8 * mm});
            skCircle(sketch, "E39.102.MirrorC", {"center": v(225, -475) * mm, "radius": 8 * mm});
            skCircle(sketch, "E39.103.MirrorC", {"center": v(-625, -225) * mm, "radius": 8 * mm});
            skCircle(sketch, "E39.104.MirrorC", {"center": v(725, -225) * mm, "radius": 8 * mm});
            skCircle(sketch, "E39.105.MirrorC", {"center": v(325, -175) * mm, "radius": 8 * mm});
            skCircle(sketch, "E39.106.MirrorC", {"center": v(275, -275) * mm, "radius": 8 * mm});
            skCircle(sketch, "E39.107.MirrorC", {"center": v(475, -175) * mm, "radius": 8 * mm});
            skCircle(sketch, "E39.108.MirrorC", {"center": v(475, -275) * mm, "radius": 8 * mm});
            skCircle(sketch, "E39.109.MirrorC", {"center": v(-125, -325) * mm, "radius": 8 * mm});
            skCircle(sketch, "E39.110.MirrorC", {"center": v(125, -375) * mm, "radius": 8 * mm});
            skCircle(sketch, "E39.111.MirrorC", {"center": v(-275, -25) * mm, "radius": 8 * mm});
            skCircle(sketch, "E39.112.MirrorC", {"center": v(325, -75) * mm, "radius": 8 * mm});
            skCircle(sketch, "E39.113.MirrorC", {"center": v(-75, -75) * mm, "radius": 8 * mm});
            skCircle(sketch, "E39.114.MirrorC", {"center": v(125, -75) * mm, "radius": 8 * mm});
            skCircle(sketch, "E39.115.MirrorC", {"center": v(-175, -275) * mm, "radius": 8 * mm});
            skCircle(sketch, "E39.116.MirrorC", {"center": v(-675, -175) * mm, "radius": 8 * mm});
            skCircle(sketch, "E39.117.MirrorC", {"center": v(175, -25) * mm, "radius": 8 * mm});
            skCircle(sketch, "E39.118.MirrorC", {"center": v(775, -25) * mm, "radius": 8 * mm});
            skCircle(sketch, "E39.119.MirrorC", {"center": v(-75, -275) * mm, "radius": 8 * mm});
            skCircle(sketch, "E39.120.MirrorC", {"center": v(-475, -75) * mm, "radius": 8 * mm});
            skCircle(sketch, "E39.121.MirrorC", {"center": v(525, -125) * mm, "radius": 8 * mm});
            skCircle(sketch, "E39.122.MirrorC", {"center": v(-175, -125) * mm, "radius": 8 * mm});
            skCircle(sketch, "E39.123.MirrorC", {"center": v(-175, -25) * mm, "radius": 8 * mm});
            skCircle(sketch, "E39.124.MirrorC", {"center": v(-625, -125) * mm, "radius": 8 * mm});
            skCircle(sketch, "E39.125.MirrorC", {"center": v(-125, -125) * mm, "radius": 8 * mm});
            skCircle(sketch, "E39.126.MirrorC", {"center": v(625, -125) * mm, "radius": 8 * mm});
            skCircle(sketch, "E39.127.MirrorC", {"center": v(425, -125) * mm, "radius": 8 * mm});
            skCircle(sketch, "E39.128.MirrorC", {"center": v(-375, -225) * mm, "radius": 8 * mm});
            skCircle(sketch, "E39.129.MirrorC", {"center": v(-625, -325) * mm, "radius": 8 * mm});
            skCircle(sketch, "E39.130.MirrorC", {"center": v(175, -375) * mm, "radius": 8 * mm});
            skCircle(sketch, "E39.131.MirrorC", {"center": v(325, -375) * mm, "radius": 8 * mm});
            skCircle(sketch, "E39.132.MirrorC", {"center": v(-525, -425) * mm, "radius": 8 * mm});
            skCircle(sketch, "E39.133.MirrorC", {"center": v(-25, -375) * mm, "radius": 8 * mm});
            skCircle(sketch, "E39.134.MirrorC", {"center": v(-375, -425) * mm, "radius": 8 * mm});
            skCircle(sketch, "E39.135.MirrorC", {"center": v(75, -475) * mm, "radius": 8 * mm});
            skCircle(sketch, "E39.136.MirrorC", {"center": v(-775, -125) * mm, "radius": 8 * mm});
            skCircle(sketch, "E39.137.MirrorC", {"center": v(-225, -125) * mm, "radius": 8 * mm});
            skCircle(sketch, "E39.138.MirrorC", {"center": v(-125, -175) * mm, "radius": 8 * mm});
            skCircle(sketch, "E39.139.MirrorC", {"center": v(-775, -225) * mm, "radius": 8 * mm});
            skCircle(sketch, "E39.140.MirrorC", {"center": v(-175, -325) * mm, "radius": 8 * mm});
            skCircle(sketch, "E39.141.MirrorC", {"center": v(-525, -325) * mm, "radius": 8 * mm});
            skCircle(sketch, "E39.142.MirrorC", {"center": v(-425, -325) * mm, "radius": 8 * mm});
            skCircle(sketch, "E39.143.MirrorC", {"center": v(525, -225) * mm, "radius": 8 * mm});
            skCircle(sketch, "E39.144.MirrorC", {"center": v(-125, -25) * mm, "radius": 8 * mm});
            skCircle(sketch, "E39.145.MirrorC", {"center": v(-625, -25) * mm, "radius": 8 * mm});
            skCircle(sketch, "E39.146.MirrorC", {"center": v(175, -75) * mm, "radius": 8 * mm});
            skCircle(sketch, "E39.147.MirrorC", {"center": v(175, -175) * mm, "radius": 8 * mm});
            skCircle(sketch, "E39.148.MirrorC", {"center": v(-325, -275) * mm, "radius": 8 * mm});
            skCircle(sketch, "E39.149.MirrorC", {"center": v(75, -225) * mm, "radius": 8 * mm});
            skCircle(sketch, "E39.150.MirrorC", {"center": v(625, -25) * mm, "radius": 8 * mm});
            skCircle(sketch, "E39.151.MirrorC", {"center": v(-225, -425) * mm, "radius": 8 * mm});
            skCircle(sketch, "E39.152.MirrorC", {"center": v(-75, -375) * mm, "radius": 8 * mm});
            skCircle(sketch, "E39.153.MirrorC", {"center": v(425, -425) * mm, "radius": 8 * mm});
            skCircle(sketch, "E39.154.MirrorC", {"center": v(125, -475) * mm, "radius": 8 * mm});
            skCircle(sketch, "E39.155.MirrorC", {"center": v(-725, -25) * mm, "radius": 8 * mm});
            skCircle(sketch, "E39.156.MirrorC", {"center": v(75, -75) * mm, "radius": 8 * mm});
            skCircle(sketch, "E39.157.MirrorC", {"center": v(575, -75) * mm, "radius": 8 * mm});
            skCircle(sketch, "E39.158.MirrorC", {"center": v(-575, -75) * mm, "radius": 8 * mm});
            skCircle(sketch, "E39.159.MirrorC", {"center": v(-125, -275) * mm, "radius": 8 * mm});
            skCircle(sketch, "E39.160.MirrorC", {"center": v(-525, -275) * mm, "radius": 8 * mm});
            skCircle(sketch, "E39.161.MirrorC", {"center": v(-275, -225) * mm, "radius": 8 * mm});
            skCircle(sketch, "E39.162.MirrorC", {"center": v(575, -275) * mm, "radius": 8 * mm});
            skCircle(sketch, "E39.163.MirrorC", {"center": v(-275, -275) * mm, "radius": 8 * mm});
            skCircle(sketch, "E39.164.MirrorC", {"center": v(375, -125) * mm, "radius": 8 * mm});
            skCircle(sketch, "E39.165.MirrorC", {"center": v(725, -275) * mm, "radius": 8 * mm});
            skCircle(sketch, "E39.166.MirrorC", {"center": v(175, -275) * mm, "radius": 8 * mm});
            skCircle(sketch, "E39.167.MirrorC", {"center": v(-275, -475) * mm, "radius": 8 * mm});
            skCircle(sketch, "E39.168.MirrorC", {"center": v(-125, -475) * mm, "radius": 8 * mm});
            skCircle(sketch, "E39.169.MirrorC", {"center": v(-225, -475) * mm, "radius": 8 * mm});
            skCircle(sketch, "E39.170.MirrorC", {"center": v(-125, -375) * mm, "radius": 8 * mm});
            skCircle(sketch, "E39.171.MirrorC", {"center": v(525, -325) * mm, "radius": 8 * mm});
            skCircle(sketch, "E39.172.MirrorC", {"center": v(-75, -325) * mm, "radius": 8 * mm});
            skCircle(sketch, "E39.173.MirrorC", {"center": v(125, -325) * mm, "radius": 8 * mm});
            skCircle(sketch, "E39.174.MirrorC", {"center": v(-475, -175) * mm, "radius": 8 * mm});
            skCircle(sketch, "E39.175.MirrorC", {"center": v(425, -175) * mm, "radius": 8 * mm});
            skCircle(sketch, "E39.176.MirrorC", {"center": v(125, -175) * mm, "radius": 8 * mm});
            skCircle(sketch, "E39.177.MirrorC", {"center": v(375, -275) * mm, "radius": 8 * mm});
            skCircle(sketch, "E39.178.MirrorC", {"center": v(325, -475) * mm, "radius": 8 * mm});
            skCircle(sketch, "E39.179.MirrorC", {"center": v(125, -425) * mm, "radius": 8 * mm});
            skCircle(sketch, "E39.180.MirrorC", {"center": v(325, -425) * mm, "radius": 8 * mm});
            skCircle(sketch, "E39.181.MirrorC", {"center": v(525, -25) * mm, "radius": 8 * mm});
            skCircle(sketch, "E39.182.MirrorC", {"center": v(425, -25) * mm, "radius": 8 * mm});
            skCircle(sketch, "E39.183.MirrorC", {"center": v(-375, -475) * mm, "radius": 8 * mm});
            skCircle(sketch, "E39.184.MirrorC", {"center": v(725, -75) * mm, "radius": 8 * mm});
            skCircle(sketch, "E39.185.MirrorC", {"center": v(-525, -75) * mm, "radius": 8 * mm});
            skCircle(sketch, "E39.186.MirrorC", {"center": v(525, -275) * mm, "radius": 8 * mm});
            skCircle(sketch, "E39.187.MirrorC", {"center": v(-325, -475) * mm, "radius": 8 * mm});
            skCircle(sketch, "E39.188.MirrorC", {"center": v(475, -125) * mm, "radius": 8 * mm});
            skCircle(sketch, "E39.189.MirrorC", {"center": v(-325, -225) * mm, "radius": 8 * mm});
            skCircle(sketch, "E39.190.MirrorC", {"center": v(-25, -275) * mm, "radius": 8 * mm});
            skCircle(sketch, "E39.191.MirrorC", {"center": v(-475, -475) * mm, "radius": 8 * mm});
            skCircle(sketch, "E39.192.MirrorC", {"center": v(-425, -475) * mm, "radius": 8 * mm});
            skCircle(sketch, "E39.193.MirrorC", {"center": v(-575, -475) * mm, "radius": 8 * mm});
            skCircle(sketch, "E39.194.MirrorC", {"center": v(-525, -475) * mm, "radius": 8 * mm});
            skCircle(sketch, "E39.195.MirrorC", {"center": v(-675, -475) * mm, "radius": 8 * mm});
            skCircle(sketch, "E39.196.MirrorC", {"center": v(-625, -475) * mm, "radius": 8 * mm});
            skCircle(sketch, "E39.197.MirrorC", {"center": v(-775, -475) * mm, "radius": 8 * mm});
            skCircle(sketch, "E39.198.MirrorC", {"center": v(-725, -475) * mm, "radius": 8 * mm});
            skCircle(sketch, "E39.199.MirrorC", {"center": v(375, -475) * mm, "radius": 8 * mm});
            skCircle(sketch, "E39.200.MirrorC", {"center": v(-275, -425) * mm, "radius": 8 * mm});
            skCircle(sketch, "E39.201.MirrorC", {"center": v(-125, -425) * mm, "radius": 8 * mm});
            skCircle(sketch, "E39.202.MirrorC", {"center": v(575, -375) * mm, "radius": 8 * mm});
            skCircle(sketch, "E39.203.MirrorC", {"center": v(425, -325) * mm, "radius": 8 * mm});
            skCircle(sketch, "E39.204.MirrorC", {"center": v(325, -325) * mm, "radius": 8 * mm});
            skCircle(sketch, "E39.205.MirrorC", {"center": v(25, -325) * mm, "radius": 8 * mm});
            skCircle(sketch, "E39.206.MirrorC", {"center": v(625, -275) * mm, "radius": 8 * mm});
            skCircle(sketch, "E39.207.MirrorC", {"center": v(75, -125) * mm, "radius": 8 * mm});
            skCircle(sketch, "E39.208.MirrorC", {"center": v(325, -125) * mm, "radius": 8 * mm});
            skCircle(sketch, "E39.209.MirrorC", {"center": v(375, -225) * mm, "radius": 8 * mm});
            skCircle(sketch, "E39.210.MirrorC", {"center": v(-225, -275) * mm, "radius": 8 * mm});
            skCircle(sketch, "E39.211.MirrorC", {"center": v(675, -125) * mm, "radius": 8 * mm});
            skCircle(sketch, "E39.212.MirrorC", {"center": v(775, -275) * mm, "radius": 8 * mm});
            skCircle(sketch, "E39.213.MirrorC", {"center": v(525, -175) * mm, "radius": 8 * mm});
            skCircle(sketch, "E39.214.MirrorC", {"center": v(75, -425) * mm, "radius": 8 * mm});
            skCircle(sketch, "E39.215.MirrorC", {"center": v(625, -475) * mm, "radius": 8 * mm});
            skCircle(sketch, "E39.216.MirrorC", {"center": v(425, -375) * mm, "radius": 8 * mm});
            skCircle(sketch, "E39.217.MirrorC", {"center": v(-775, -425) * mm, "radius": 8 * mm});
            skCircle(sketch, "E39.218.MirrorC", {"center": v(-775, -325) * mm, "radius": 8 * mm});
            skCircle(sketch, "E39.219.MirrorC", {"center": v(-475, -375) * mm, "radius": 8 * mm});
            skCircle(sketch, "E39.220.MirrorC", {"center": v(275, -175) * mm, "radius": 8 * mm});
            skCircle(sketch, "E39.221.MirrorC", {"center": v(-325, -325) * mm, "radius": 8 * mm});
            skCircle(sketch, "E39.222.MirrorC", {"center": v(-25, -75) * mm, "radius": 8 * mm});
            skCircle(sketch, "E39.223.MirrorC", {"center": v(625, -75) * mm, "radius": 8 * mm});
            skCircle(sketch, "E39.224.MirrorC", {"center": v(-725, -225) * mm, "radius": 8 * mm});
            skCircle(sketch, "E39.225.MirrorC", {"center": v(425, -475) * mm, "radius": 8 * mm});
            skCircle(sketch, "E39.226.MirrorC", {"center": v(525, -425) * mm, "radius": 8 * mm});
            skCircle(sketch, "E39.227.MirrorC", {"center": v(675, -425) * mm, "radius": 8 * mm});
            skCircle(sketch, "E39.228.MirrorC", {"center": v(325, -25) * mm, "radius": 8 * mm});
            skCircle(sketch, "E39.229.MirrorC", {"center": v(-475, -125) * mm, "radius": 8 * mm});
            skCircle(sketch, "E39.230.MirrorC", {"center": v(775, -225) * mm, "radius": 8 * mm});
            skCircle(sketch, "E39.231.MirrorC", {"center": v(-625, -175) * mm, "radius": 8 * mm});
            skCircle(sketch, "E39.232.MirrorC", {"center": v(425, -225) * mm, "radius": 8 * mm});
            skCircle(sketch, "E39.233.MirrorC", {"center": v(675, -175) * mm, "radius": 8 * mm});
            skCircle(sketch, "E39.234.MirrorC", {"center": v(575, -225) * mm, "radius": 8 * mm});
            skCircle(sketch, "E39.235.MirrorC", {"center": v(-425, -25) * mm, "radius": 8 * mm});
            skCircle(sketch, "E39.236.MirrorC", {"center": v(475, -225) * mm, "radius": 8 * mm});
            skCircle(sketch, "E39.237.MirrorC", {"center": v(-125, -225) * mm, "radius": 8 * mm});
            skCircle(sketch, "E39.238.MirrorC", {"center": v(-775, -175) * mm, "radius": 8 * mm});
            skCircle(sketch, "E39.239.MirrorC", {"center": v(325, -275) * mm, "radius": 8 * mm});
            skCircle(sketch, "E39.240.MirrorC", {"center": v(-575, -25) * mm, "radius": 8 * mm});
            skCircle(sketch, "E39.241.MirrorC", {"center": v(675, -475) * mm, "radius": 8 * mm});
            skCircle(sketch, "E39.242.MirrorC", {"center": v(-175, -425) * mm, "radius": 8 * mm});
            skCircle(sketch, "E39.243.MirrorC", {"center": v(-625, -425) * mm, "radius": 8 * mm});
            skCircle(sketch, "E39.244.MirrorC", {"center": v(-225, -375) * mm, "radius": 8 * mm});
            skCircle(sketch, "E39.245.MirrorC", {"center": v(75, -325) * mm, "radius": 8 * mm});
            skCircle(sketch, "E39.246.MirrorC", {"center": v(-725, -325) * mm, "radius": 8 * mm});
            skCircle(sketch, "E39.247.MirrorC", {"center": v(-675, -375) * mm, "radius": 8 * mm});
            skCircle(sketch, "E39.248.MirrorC", {"center": v(225, -125) * mm, "radius": 8 * mm});
            skCircle(sketch, "E39.249.MirrorC", {"center": v(-375, -175) * mm, "radius": 8 * mm});
            skCircle(sketch, "E39.250.MirrorC", {"center": v(-425, -125) * mm, "radius": 8 * mm});
            skCircle(sketch, "E39.251.MirrorC", {"center": v(625, -175) * mm, "radius": 8 * mm});
            skCircle(sketch, "E39.252.MirrorC", {"center": v(-175, -175) * mm, "radius": 8 * mm});
            skCircle(sketch, "E39.253.MirrorC", {"center": v(25, -125) * mm, "radius": 8 * mm});
            skCircle(sketch, "E39.254.MirrorC", {"center": v(625, -225) * mm, "radius": 8 * mm});
            skCircle(sketch, "E39.255.MirrorC", {"center": v(25, -75) * mm, "radius": 8 * mm});
            skCircle(sketch, "E39.256.MirrorC", {"center": v(-325, -75) * mm, "radius": 8 * mm});
            skCircle(sketch, "E39.257.MirrorC", {"center": v(575, -175) * mm, "radius": 8 * mm});
            skCircle(sketch, "E39.258.MirrorC", {"center": v(-125, -75) * mm, "radius": 8 * mm});
            skCircle(sketch, "E39.259.MirrorC", {"center": v(475, -25) * mm, "radius": 8 * mm});
            skCircle(sketch, "E39.260.MirrorC", {"center": v(225, -25) * mm, "radius": 8 * mm});
            skCircle(sketch, "E39.261.MirrorC", {"center": v(125, -25) * mm, "radius": 8 * mm});
            skCircle(sketch, "E39.262.MirrorC", {"center": v(-225, -25) * mm, "radius": 8 * mm});
            skCircle(sketch, "E39.263.MirrorC", {"center": v(225, -375) * mm, "radius": 8 * mm});
            skCircle(sketch, "E39.264.MirrorC", {"center": v(-575, -375) * mm, "radius": 8 * mm});
            skCircle(sketch, "E39.265.MirrorC", {"center": v(-425, -375) * mm, "radius": 8 * mm});
            skCircle(sketch, "E39.266.MirrorC", {"center": v(775, -375) * mm, "radius": 8 * mm});
            skCircle(sketch, "E39.267.MirrorC", {"center": v(475, -475) * mm, "radius": 8 * mm});
            skCircle(sketch, "E39.268.MirrorC", {"center": v(775, -425) * mm, "radius": 8 * mm});
            skCircle(sketch, "E39.269.MirrorC", {"center": v(-325, -425) * mm, "radius": 8 * mm});
            skCircle(sketch, "E39.270.MirrorC", {"center": v(275, -475) * mm, "radius": 8 * mm});
            skCircle(sketch, "E39.271.MirrorC", {"center": v(-25, -325) * mm, "radius": 8 * mm});
            skCircle(sketch, "E39.272.MirrorC", {"center": v(-225, -325) * mm, "radius": 8 * mm});
            skCircle(sketch, "E39.273.MirrorC", {"center": v(725, -375) * mm, "radius": 8 * mm});
            skCircle(sketch, "E39.274.MirrorC", {"center": v(-275, -375) * mm, "radius": 8 * mm});
            skCircle(sketch, "E39.275.MirrorC", {"center": v(175, -125) * mm, "radius": 8 * mm});
            skCircle(sketch, "E39.276.MirrorC", {"center": v(-525, -225) * mm, "radius": 8 * mm});
            skCircle(sketch, "E39.277.MirrorC", {"center": v(525, -75) * mm, "radius": 8 * mm});
            skCircle(sketch, "E39.278.MirrorC", {"center": v(-775, -25) * mm, "radius": 8 * mm});
            skCircle(sketch, "E39.279.MirrorC", {"center": v(25, -275) * mm, "radius": 8 * mm});
            skCircle(sketch, "E39.280.MirrorC", {"center": v(675, -75) * mm, "radius": 8 * mm});
            skCircle(sketch, "E39.281.MirrorC", {"center": v(475, -75) * mm, "radius": 8 * mm});
            skCircle(sketch, "E39.282.MirrorC", {"center": v(-175, -75) * mm, "radius": 8 * mm});
            skCircle(sketch, "E39.283.MirrorC", {"center": v(-175, -225) * mm, "radius": 8 * mm});
            skCircle(sketch, "E39.284.MirrorC", {"center": v(75, -375) * mm, "radius": 8 * mm});
            skCircle(sketch, "E39.285.MirrorC", {"center": v(625, -375) * mm, "radius": 8 * mm});
            skCircle(sketch, "E39.286.MirrorC", {"center": v(775, -125) * mm, "radius": 8 * mm});
            skCircle(sketch, "E39.287.MirrorC", {"center": v(-575, -275) * mm, "radius": 8 * mm});
            skCircle(sketch, "E39.288.MirrorC", {"center": v(675, -225) * mm, "radius": 8 * mm});
            skCircle(sketch, "E39.289.MirrorC", {"center": v(-225, -175) * mm, "radius": 8 * mm});
            skCircle(sketch, "E39.290.MirrorC", {"center": v(-375, -275) * mm, "radius": 8 * mm});
            skCircle(sketch, "E39.291.MirrorC", {"center": v(-475, -25) * mm, "radius": 8 * mm});
            skCircle(sketch, "E39.292.MirrorC", {"center": v(-675, -75) * mm, "radius": 8 * mm});
            skCircle(sketch, "E39.293.MirrorC", {"center": v(25, -175) * mm, "radius": 8 * mm});
            skCircle(sketch, "E39.294.MirrorC", {"center": v(-775, -275) * mm, "radius": 8 * mm});
            skCircle(sketch, "E39.295.MirrorC", {"center": v(-325, -175) * mm, "radius": 8 * mm});
            skCircle(sketch, "E39.296.MirrorC", {"center": v(625, -425) * mm, "radius": 8 * mm});
            skCircle(sketch, "E39.297.MirrorC", {"center": v(-325, -25) * mm, "radius": 8 * mm});
            skCircle(sketch, "E39.298.MirrorC", {"center": v(775, -325) * mm, "radius": 8 * mm});
            skCircle(sketch, "E39.299.MirrorC", {"center": v(-375, -325) * mm, "radius": 8 * mm});
            skCircle(sketch, "E39.300.MirrorC", {"center": v(-25, -25) * mm, "radius": 8 * mm});
            skCircle(sketch, "E39.301.MirrorC", {"center": v(-325, -375) * mm, "radius": 8 * mm});
            skCircle(sketch, "E39.302.MirrorC", {"center": v(-625, -375) * mm, "radius": 8 * mm});
            skCircle(sketch, "E39.303.MirrorC", {"center": v(225, -425) * mm, "radius": 8 * mm});
            skCircle(sketch, "E39.304.MirrorC", {"center": v(125, -225) * mm, "radius": 8 * mm});
            skCircle(sketch, "E39.305.MirrorC", {"center": v(775, -175) * mm, "radius": 8 * mm});
            skCircle(sketch, "E39.306.MirrorC", {"center": v(375, -25) * mm, "radius": 8 * mm});
            skCircle(sketch, "E39.307.MirrorC", {"center": v(525, -475) * mm, "radius": 8 * mm});
            skCircle(sketch, "E39.308.MirrorC", {"center": v(-575, -425) * mm, "radius": 8 * mm});
            skCircle(sketch, "E39.309.MirrorC", {"center": v(575, -425) * mm, "radius": 8 * mm});
            skCircle(sketch, "E39.310.MirrorC", {"center": v(-25, -225) * mm, "radius": 8 * mm});
            skCircle(sketch, "E39.311.MirrorC", {"center": v(-375, -125) * mm, "radius": 8 * mm});
            skCircle(sketch, "E39.312.MirrorC", {"center": v(-575, -225) * mm, "radius": 8 * mm});
            skCircle(sketch, "E39.313.MirrorC", {"center": v(-275, -75) * mm, "radius": 8 * mm});
            skCircle(sketch, "E39.314.MirrorC", {"center": v(-375, -75) * mm, "radius": 8 * mm});
            skCircle(sketch, "E39.315.MirrorC", {"center": v(-475, -275) * mm, "radius": 8 * mm});
            skCircle(sketch, "E39.316.MirrorC", {"center": v(125, -275) * mm, "radius": 8 * mm});
            skCircle(sketch, "E39.317.MirrorC", {"center": v(-775, -375) * mm, "radius": 8 * mm});
            skCircle(sketch, "E39.318.MirrorC", {"center": v(575, -325) * mm, "radius": 8 * mm});
            skCircle(sketch, "E39.319.MirrorC", {"center": v(225, -275) * mm, "radius": 8 * mm});
            skSolve(sketch);
        }
        {
            var Q0;
            Q0=makeQuery(id+"F0.imprint","IMPRINT",FACE,{"disambiguationData":[TD([[makeQuery(id+"F0.imprint","IMPRINT",EDGE,{"derivedFrom":sQuery(id+"F0.wireOp",EDGE,"E0.rect.top")}),1.0]])]});
            extrude(context, id + "F1", {"entities" : qUnion([Q0]), "depth" : 16 * mm});
        }
        {
            var Q0;
            Q0=makeQuery(id+"F1.opExtrude","SWEPT_EDGE",EDGE,{"disambiguationData":[OSD([sQuery(id+"F0.wireOp",EDGE,"E0.rect.top"),sQuery(id+"F0.wireOp",EDGE,"E0.rect.right")])]});
            var Q1;
            Q1=makeQuery(id+"F1.opExtrude","SWEPT_EDGE",EDGE,{"disambiguationData":[OSD([sQuery(id+"F0.wireOp",EDGE,"E0.rect.right"),sQuery(id+"F0.wireOp",EDGE,"E34")])]});
            var Q2;
            Q2=makeQuery(id+"F1.opExtrude","SWEPT_EDGE",EDGE,{"disambiguationData":[OSD([sQuery(id+"F0.wireOp",EDGE,"E0.rect.left"),sQuery(id+"F0.wireOp",EDGE,"E34")])]});
            var Q3;
            Q3=makeQuery(id+"F1.opExtrude","SWEPT_EDGE",EDGE,{"disambiguationData":[OSD([sQuery(id+"F0.wireOp",EDGE,"E0.rect.top"),sQuery(id+"F0.wireOp",EDGE,"E0.rect.left")])]});
            fillet(context, id + "F2", {"entities" : qUnion([Q0, Q1, Q2, Q3]), "radius" : 10 * mm, "tangentPropagation" : true, "allowEdgeOverflow" : false});
        }
    });
